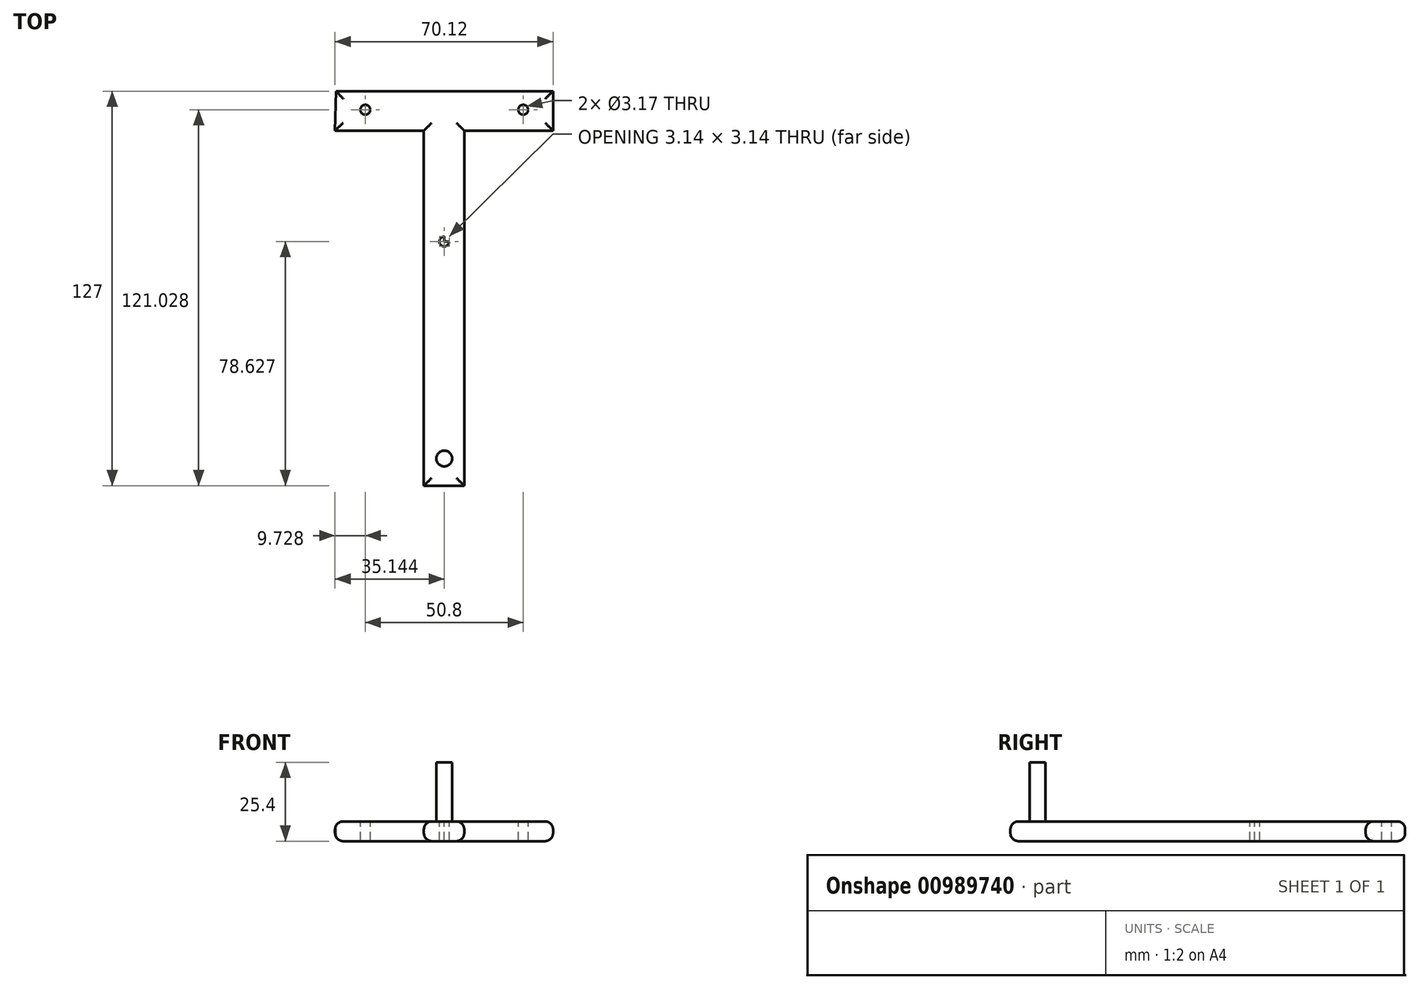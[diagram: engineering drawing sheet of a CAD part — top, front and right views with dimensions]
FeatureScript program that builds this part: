
annotation { "Feature Type Name" : "Feature", "Feature Type Description" : "" }
export const myFeature = defineFeature(function(context is Context, id is Id, definition is map)
    precondition{}
    {
        {
            var Q0;
            Q0=qCreatedBy(makeId("Top.planeOp"),FACE);
            var sketch = newSketch(context, id + "F0", { "sketchPlane" : qUnion([Q0])});
            skLineSegment(sketch, "E0", {"start": v(-38.73, 114.3) * mm, "end": v(31.12, 114.3) * mm});
            skLineSegment(sketch, "E1", {"start": v(31.12, 114.3) * mm, "end": v(31.12, 101.6) * mm});
            skLineSegment(sketch, "E2", {"start": v(31.12, 101.6) * mm, "end": v(2.54, 101.6) * mm});
            skLineSegment(sketch, "E3", {"start": v(2.54, 101.6) * mm, "end": v(2.54, -12.7) * mm});
            skLineSegment(sketch, "E4", {"start": v(2.54, -12.7) * mm, "end": v(-10.43, -12.7) * mm});
            skLineSegment(sketch, "E5", {"start": v(-10.43, -12.7) * mm, "end": v(-10.43, 101.6) * mm});
            skLineSegment(sketch, "E6", {"start": v(-10.43, 101.6) * mm, "end": v(-39, 101.6) * mm});
            skLineSegment(sketch, "E7", {"start": v(-39, 101.6) * mm, "end": v(-38.73, 114.3) * mm});
            skSolve(sketch);
        }
        {
            var Q0;
            Q0 = qSketchRegion(id + "F0", true);
            extrude(context, id + "F1", {"entities" : qUnion([Q0]), "depth" : 6.35 * mm, "offsetDistance" : 25.4 * mm});
        }
        {
            var Q0;
            Q0=makeQuery(id+"F1.opExtrude","CAP_FACE",FACE,{"disambiguationData":[OSD([sQuery(id+"F0.wireOp",EDGE,"E0"),sQuery(id+"F0.wireOp",EDGE,"E1"),sQuery(id+"F0.wireOp",EDGE,"E2"),sQuery(id+"F0.wireOp",EDGE,"E3"),sQuery(id+"F0.wireOp",EDGE,"E4"),sQuery(id+"F0.wireOp",EDGE,"E5"),sQuery(id+"F0.wireOp",EDGE,"E6"),sQuery(id+"F0.wireOp",EDGE,"E7")])],"isStart":false});
            var sketch = newSketch(context, id + "F2", { "sketchPlane" : qUnion([Q0])});
            skLineSegment(sketch, "E8", {"start": v(-29.27, 108.33) * mm, "end": v(21.53, 108.33) * mm});
            skLineSegment(sketch, "E9", {"start": v(-29.27, 108.33) * mm, "end": v(-38.86, 108.33) * mm});
            skLineSegment(sketch, "E10", {"start": v(21.53, 108.33) * mm, "end": v(31.12, 108.33) * mm});
            skCircle(sketch, "E11", {"center": v(-29.27, 108.33) * mm, "radius": 1.59 * mm});
            skCircle(sketch, "E12", {"center": v(21.53, 108.33) * mm, "radius": 1.59 * mm});
            skCircle(sketch, "E13", {"center": v(-3.87, 65.91) * mm, "radius": 1.59 * mm});
            skLineSegment(sketch, "E14", {"start": v(-3.87, 108.33) * mm, "end": v(-3.87, -12.7) * mm});
            skLineSegment(sketch, "E15", {"start": v(21.71, 109.9) * mm, "end": v(21.71, 65.91) * mm});
            skLineSegment(sketch, "E16", {"start": v(21.71, 65.91) * mm, "end": v(-3.87, 65.91) * mm});
            skLineSegment(sketch, "E17", {"start": v(11.67, 65.91) * mm, "end": v(11.67, -3.94) * mm});
            skCircle(sketch, "E18", {"center": v(-3.87, -3.94) * mm, "radius": 2.54 * mm});
            skLineSegment(sketch, "E19", {"start": v(11.67, -3.94) * mm, "end": v(-3.87, -3.94) * mm});
            skSolve(sketch);
        }
        {
            var Q0;
            Q0=makeQuery(id+"F1.opExtrude","CAP_EDGE",EDGE,{"disambiguationData":[OSD([sQuery(id+"F0.wireOp",EDGE,"E6")])],"isStart":false});
            var Q1;
            Q1=makeQuery(id+"F1.opExtrude","CAP_EDGE",EDGE,{"disambiguationData":[OSD([sQuery(id+"F0.wireOp",EDGE,"E7")])],"isStart":false});
            var Q2;
            Q2=makeQuery(id+"F1.opExtrude","CAP_EDGE",EDGE,{"disambiguationData":[OSD([sQuery(id+"F0.wireOp",EDGE,"E0")])],"isStart":false});
            var Q3;
            Q3=makeQuery(id+"F1.opExtrude","CAP_EDGE",EDGE,{"disambiguationData":[OSD([sQuery(id+"F0.wireOp",EDGE,"E2")])],"isStart":false});
            var Q4;
            Q4=makeQuery(id+"F1.opExtrude","CAP_EDGE",EDGE,{"disambiguationData":[OSD([sQuery(id+"F0.wireOp",EDGE,"E1")])],"isStart":false});
            var Q5;
            Q5=makeQuery(id+"F1.opExtrude","CAP_EDGE",EDGE,{"disambiguationData":[OSD([sQuery(id+"F0.wireOp",EDGE,"E3")])],"isStart":false});
            var Q6;
            Q6=makeQuery(id+"F1.opExtrude","CAP_EDGE",EDGE,{"disambiguationData":[OSD([sQuery(id+"F0.wireOp",EDGE,"E5")])],"isStart":false});
            var Q7;
            Q7=makeQuery(id+"F1.opExtrude","CAP_EDGE",EDGE,{"disambiguationData":[OSD([sQuery(id+"F0.wireOp",EDGE,"E4")])],"isStart":false});
            var Q8;
            Q8=makeQuery(id+"F1.opExtrude","CAP_EDGE",EDGE,{"disambiguationData":[OSD([sQuery(id+"F0.wireOp",EDGE,"E6")])],"isStart":true});
            var Q9;
            Q9=makeQuery(id+"F1.opExtrude","CAP_EDGE",EDGE,{"disambiguationData":[OSD([sQuery(id+"F0.wireOp",EDGE,"E7")])],"isStart":true});
            var Q10;
            Q10=makeQuery(id+"F1.opExtrude","CAP_EDGE",EDGE,{"disambiguationData":[OSD([sQuery(id+"F0.wireOp",EDGE,"E0")])],"isStart":true});
            var Q11;
            Q11=makeQuery(id+"F1.opExtrude","CAP_EDGE",EDGE,{"disambiguationData":[OSD([sQuery(id+"F0.wireOp",EDGE,"E2")])],"isStart":true});
            var Q12;
            Q12=makeQuery(id+"F1.opExtrude","CAP_EDGE",EDGE,{"disambiguationData":[OSD([sQuery(id+"F0.wireOp",EDGE,"E1")])],"isStart":true});
            var Q13;
            Q13=makeQuery(id+"F1.opExtrude","CAP_EDGE",EDGE,{"disambiguationData":[OSD([sQuery(id+"F0.wireOp",EDGE,"E3")])],"isStart":true});
            var Q14;
            Q14=makeQuery(id+"F1.opExtrude","CAP_EDGE",EDGE,{"disambiguationData":[OSD([sQuery(id+"F0.wireOp",EDGE,"E5")])],"isStart":true});
            var Q15;
            Q15=makeQuery(id+"F1.opExtrude","CAP_EDGE",EDGE,{"disambiguationData":[OSD([sQuery(id+"F0.wireOp",EDGE,"E4")])],"isStart":true});
            fillet(context, id + "F3", {"entities" : qUnion([Q0, Q1, Q2, Q3, Q4, Q5, Q6, Q7, Q8, Q9, Q10, Q11, Q12, Q13, Q14, Q15]), "radius" : 2.54 * mm, "tangentPropagation" : true, "allowEdgeOverflow" : false});
        }
        {
            var Q0;
            {var subQ0=sQuery(id+"F2.wireOp",EDGE,"E9");var subQ1=sQuery(id+"F2.wireOp",EDGE,"E8");var subQ2=makeQuery(id+"F2.imprint","INTERSECT",VERTEX,{"derivedFrom":[subQ1,subQ0]});Q0=makeQuery(id+"F2.imprint","IMPRINT",FACE,{"disambiguationData":[TD([[makeQuery(id+"F2.imprint","IMPRINT",EDGE,{"disambiguationData":[TD([[subQ2,-1.0]])],"derivedFrom":subQ1}),-1.0]])]});}
            var Q1;
            {var subQ0=sQuery(id+"F2.wireOp",EDGE,"E9");var subQ1=sQuery(id+"F2.wireOp",EDGE,"E8");var subQ2=makeQuery(id+"F2.imprint","INTERSECT",VERTEX,{"derivedFrom":[subQ1,subQ0]});Q1=makeQuery(id+"F2.imprint","IMPRINT",FACE,{"disambiguationData":[TD([[makeQuery(id+"F2.imprint","IMPRINT",EDGE,{"disambiguationData":[TD([[subQ2,-1.0]])],"derivedFrom":subQ1}),1.0]])]});}
            extrude(context, id + "F4", {"entities" : qUnion([Q0, Q1]), "operationType" : NewBodyOperationType.REMOVE, "oppositeDirection" : true, "depth" : 6.35 * mm, "offsetDistance" : 25.4 * mm});
        }
        {
            var Q0;
            {var subQ0=sQuery(id+"F2.wireOp",EDGE,"E10");var subQ1=sQuery(id+"F2.wireOp",EDGE,"E8");var subQ2=makeQuery(id+"F2.imprint","INTERSECT",VERTEX,{"derivedFrom":[subQ1,subQ0]});Q0=makeQuery(id+"F2.imprint","IMPRINT",FACE,{"disambiguationData":[TD([[makeQuery(id+"F2.imprint","IMPRINT",EDGE,{"disambiguationData":[TD([[subQ2,1.0]])],"derivedFrom":subQ1}),1.0]])]});}
            var Q1;
            {var subQ0=sQuery(id+"F2.wireOp",EDGE,"E15");var subQ1=sQuery(id+"F2.wireOp",EDGE,"E10");var subQ2=makeQuery(id+"F2.imprint","INTERSECT",VERTEX,{"derivedFrom":[subQ1,subQ0]});Q1=makeQuery(id+"F2.imprint","IMPRINT",FACE,{"disambiguationData":[TD([[makeQuery(id+"F2.imprint","IMPRINT",EDGE,{"disambiguationData":[TD([[subQ2,-1.0]])],"derivedFrom":subQ1}),1.0]])]});}
            var Q2;
            {var subQ0=sQuery(id+"F2.wireOp",EDGE,"E15");var subQ1=sQuery(id+"F2.wireOp",EDGE,"E10");var subQ2=makeQuery(id+"F2.imprint","INTERSECT",VERTEX,{"derivedFrom":[subQ1,subQ0]});Q2=makeQuery(id+"F2.imprint","IMPRINT",FACE,{"disambiguationData":[TD([[makeQuery(id+"F2.imprint","IMPRINT",EDGE,{"disambiguationData":[TD([[subQ2,-1.0]])],"derivedFrom":subQ1}),-1.0]])]});}
            var Q3;
            {var subQ0=sQuery(id+"F2.wireOp",EDGE,"E10");var subQ1=sQuery(id+"F2.wireOp",EDGE,"E8");var subQ2=makeQuery(id+"F2.imprint","INTERSECT",VERTEX,{"derivedFrom":[subQ1,subQ0]});Q3=makeQuery(id+"F2.imprint","IMPRINT",FACE,{"disambiguationData":[TD([[makeQuery(id+"F2.imprint","IMPRINT",EDGE,{"disambiguationData":[TD([[subQ2,1.0]])],"derivedFrom":subQ1}),-1.0]])]});}
            extrude(context, id + "F5", {"entities" : qUnion([Q0, Q1, Q2, Q3]), "operationType" : NewBodyOperationType.REMOVE, "oppositeDirection" : true, "depth" : 6.35 * mm, "offsetDistance" : 25.4 * mm});
        }
        {
            var Q0;
            {var subQ0=sQuery(id+"F2.wireOp",EDGE,"E14");var subQ1=sQuery(id+"F2.wireOp",EDGE,"E13");var subQ2=makeQuery(id+"F2.imprint","INTERSECT",VERTEX,{"disambiguationData":[OD(0.0)],"derivedFrom":[subQ1,subQ0]});Q0=makeQuery(id+"F2.imprint","IMPRINT",FACE,{"disambiguationData":[TD([[makeQuery(id+"F2.imprint","IMPRINT",EDGE,{"disambiguationData":[TD([[subQ2,-1.0]])],"derivedFrom":subQ1}),1.0]])]});}
            var Q1;
            {var subQ0=sQuery(id+"F2.wireOp",EDGE,"E14");var subQ1=sQuery(id+"F2.wireOp",EDGE,"E13");var subQ2=makeQuery(id+"F2.imprint","INTERSECT",VERTEX,{"disambiguationData":[OD(0.0)],"derivedFrom":[subQ1,subQ0]});Q1=makeQuery(id+"F2.imprint","IMPRINT",FACE,{"disambiguationData":[TD([[makeQuery(id+"F2.imprint","IMPRINT",EDGE,{"disambiguationData":[TD([[subQ2,1.0]])],"derivedFrom":subQ1}),1.0]])]});}
            var Q2;
            {var subQ0=sQuery(id+"F2.wireOp",EDGE,"E16");var subQ1=sQuery(id+"F2.wireOp",EDGE,"E13");var subQ2=makeQuery(id+"F2.imprint","INTERSECT",VERTEX,{"derivedFrom":[subQ1,subQ0]});Q2=makeQuery(id+"F2.imprint","IMPRINT",FACE,{"disambiguationData":[TD([[makeQuery(id+"F2.imprint","IMPRINT",EDGE,{"disambiguationData":[TD([[subQ2,1.0]])],"derivedFrom":subQ1}),1.0]])]});}
            extrude(context, id + "F6", {"entities" : qUnion([Q0, Q1, Q2]), "operationType" : NewBodyOperationType.REMOVE, "oppositeDirection" : true, "depth" : 6.35 * mm, "offsetDistance" : 25.4 * mm});
        }
        {
            var Q0;
            {var subQ0=sQuery(id+"F2.wireOp",EDGE,"E14");var subQ1=makeQuery(id+"F2.imprint","INTERSECT",VERTEX,{"derivedFrom":[subQ0,sQuery(id+"F2.wireOp",EDGE,"E19")]});Q0=makeQuery(id+"F2.imprint","IMPRINT",FACE,{"disambiguationData":[TD([[makeQuery(id+"F2.imprint","IMPRINT",EDGE,{"disambiguationData":[TD([[subQ1,1.0]])],"derivedFrom":subQ0}),-1.0]])]});}
            var Q1;
            {var subQ0=sQuery(id+"F2.wireOp",EDGE,"E19");var subQ1=sQuery(id+"F2.wireOp",EDGE,"E14");var subQ2=makeQuery(id+"F2.imprint","INTERSECT",VERTEX,{"derivedFrom":[subQ1,subQ0]});Q1=makeQuery(id+"F2.imprint","IMPRINT",FACE,{"disambiguationData":[TD([[makeQuery(id+"F2.imprint","IMPRINT",EDGE,{"disambiguationData":[TD([[subQ2,1.0]])],"derivedFrom":subQ1}),1.0]])]});}
            var Q2;
            {var subQ0=sQuery(id+"F2.wireOp",EDGE,"E19");var subQ1=sQuery(id+"F2.wireOp",EDGE,"E14");var subQ2=makeQuery(id+"F2.imprint","INTERSECT",VERTEX,{"derivedFrom":[subQ1,subQ0]});Q2=makeQuery(id+"F2.imprint","IMPRINT",FACE,{"disambiguationData":[TD([[makeQuery(id+"F2.imprint","IMPRINT",EDGE,{"disambiguationData":[TD([[subQ2,-1.0]])],"derivedFrom":subQ1}),1.0]])]});}
            extrude(context, id + "F7", {"entities" : qUnion([Q0, Q1, Q2]), "operationType" : NewBodyOperationType.ADD, "depth" : 19.05 * mm, "offsetDistance" : 25.4 * mm});
        }
    });
